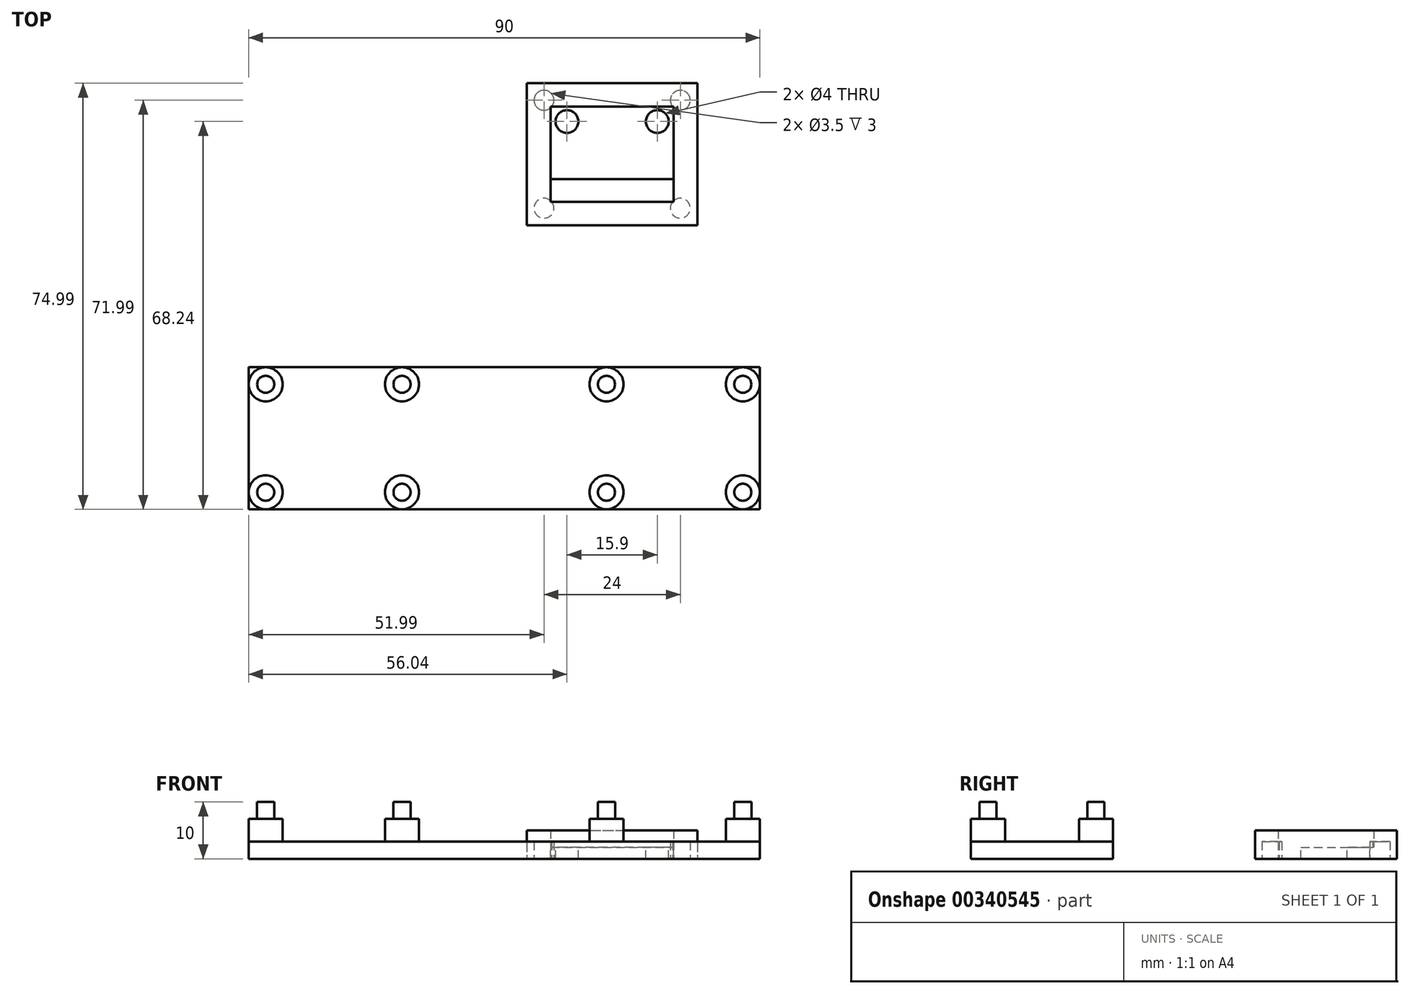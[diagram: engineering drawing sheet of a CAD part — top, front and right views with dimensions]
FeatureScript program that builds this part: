
annotation { "Feature Type Name" : "Feature", "Feature Type Description" : "" }
export const myFeature = defineFeature(function(context is Context, id is Id, definition is map)
    precondition{}
    {
        {
            var Q0;
            Q0=qCreatedBy(makeId("Top.planeOp"),FACE);
            var sketch = newSketch(context, id + "F0", { "sketchPlane" : qUnion([Q0])});
            skLineSegment(sketch, "E0.bottom", {"start": v(-15, 12.5) * mm, "end": v(15, 12.5) * mm});
            skLineSegment(sketch, "E0.top", {"start": v(-15, -12.5) * mm, "end": v(15, -12.5) * mm});
            skLineSegment(sketch, "E0.left", {"start": v(-15, 12.5) * mm, "end": v(-15, -12.5) * mm});
            skLineSegment(sketch, "E0.right", {"start": v(15, 12.5) * mm, "end": v(15, -12.5) * mm});
            skLineSegment(sketch, "E1.bottom", {"start": v(-10.8, 8.4) * mm, "end": v(10.8, 8.4) * mm});
            skLineSegment(sketch, "E1.top", {"start": v(-10.8, -8.4) * mm, "end": v(10.8, -8.4) * mm});
            skLineSegment(sketch, "E1.left", {"start": v(-10.8, 8.4) * mm, "end": v(-10.8, -8.4) * mm});
            skLineSegment(sketch, "E1.right", {"start": v(10.8, 8.4) * mm, "end": v(10.8, -8.4) * mm});
            skLineSegment(sketch, "E2", {"start": v(-15, 12.5) * mm, "end": v(15, -12.5) * mm, "construction": true});
            skLineSegment(sketch, "E3", {"start": v(-15, -12.5) * mm, "end": v(15, 12.5) * mm, "construction": true});
            skLineSegment(sketch, "E4", {"start": v(-10.8, 8.4) * mm, "end": v(10.8, -8.4) * mm, "construction": true});
            skLineSegment(sketch, "E5", {"start": v(-10.8, -8.4) * mm, "end": v(10.8, 8.4) * mm, "construction": true});
            skPoint(sketch, "E6", {"position": v(0, 0) * mm});
            skSolve(sketch);
        }
        {
            var Q0;
            Q0=qSketchRegion(id+"F0",true);
            extrude(context, id + "F1", {"entities" : qUnion([Q0]), "depth" : 5 * mm});
        }
        {
            var Q0;
            Q0=makeQuery(id+"F1.opExtrude","CAP_FACE",FACE,{"disambiguationData":[OSD([sQuery(id+"F0.wireOp",EDGE,"E0.bottom"),sQuery(id+"F0.wireOp",EDGE,"E0.top"),sQuery(id+"F0.wireOp",EDGE,"E0.left"),sQuery(id+"F0.wireOp",EDGE,"E0.right"),sQuery(id+"F0.wireOp",EDGE,"E1.bottom"),sQuery(id+"F0.wireOp",EDGE,"E1.top"),sQuery(id+"F0.wireOp",EDGE,"E1.left"),sQuery(id+"F0.wireOp",EDGE,"E1.right")])],"isStart":true});
            var sketch = newSketch(context, id + "F2", { "sketchPlane" : qUnion([Q0])});
            skLineSegment(sketch, "E7.0", {"start": v(-15, 12.5) * mm, "end": v(15, 12.5) * mm});
            skLineSegment(sketch, "E8.0", {"start": v(-15, -12.5) * mm, "end": v(-15, 12.5) * mm});
            skLineSegment(sketch, "E9.0", {"start": v(-15, -12.5) * mm, "end": v(15, -12.5) * mm});
            skLineSegment(sketch, "E10.0", {"start": v(15, -12.5) * mm, "end": v(15, 12.5) * mm});
            skSolve(sketch);
        }
        {
            var Q0;
            Q0=qSketchRegion(id+"F2",true);
            extrude(context, id + "F3", {"entities" : qUnion([Q0]), "operationType" : NewBodyOperationType.ADD, "oppositeDirection" : true, "depth" : 2 * mm});
        }
        {
            var Q0;
            Q0=makeQuery(id+"F3.opExtrude","CAP_FACE",FACE,{"disambiguationData":[OSD([sQuery(id+"F2.wireOp",EDGE,"E7.0"),sQuery(id+"F2.wireOp",EDGE,"E8.0"),sQuery(id+"F2.wireOp",EDGE,"E9.0"),sQuery(id+"F2.wireOp",EDGE,"E10.0")])],"isStart":false});
            var sketch = newSketch(context, id + "F4", { "sketchPlane" : qUnion([Q0])});
            skLineSegment(sketch, "E11.bottom", {"start": v(-10.8, -8.4) * mm, "end": v(10.8, -8.4) * mm});
            skLineSegment(sketch, "E11.top", {"start": v(-10.8, -4.4) * mm, "end": v(10.8, -4.4) * mm});
            skLineSegment(sketch, "E11.left", {"start": v(-10.8, -8.4) * mm, "end": v(-10.8, -4.4) * mm});
            skLineSegment(sketch, "E11.right", {"start": v(10.8, -8.4) * mm, "end": v(10.8, -4.4) * mm});
            skSolve(sketch);
        }
        {
            var Q0;
            Q0=qSketchRegion(id+"F4",true);
            extrude(context, id + "F5", {"entities" : qUnion([Q0]), "operationType" : NewBodyOperationType.REMOVE, "endBound" : BoundingType.UP_TO_NEXT, "oppositeDirection" : true, "depth" : 1.5 * mm});
        }
        {
            var Q0;
            Q0=makeQuery(id+"F3.opExtrude","CAP_FACE",FACE,{"disambiguationData":[OSD([sQuery(id+"F2.wireOp",EDGE,"E7.0"),sQuery(id+"F2.wireOp",EDGE,"E8.0"),sQuery(id+"F2.wireOp",EDGE,"E9.0"),sQuery(id+"F2.wireOp",EDGE,"E10.0")])],"isStart":false});
            var sketch = newSketch(context, id + "F6", { "sketchPlane" : qUnion([Q0])});
            skLineSegment(sketch, "E12", {"start": v(-7.95, 5.75) * mm, "end": v(7.95, 5.75) * mm, "construction": true});
            skCircle(sketch, "E13", {"center": v(-7.95, 5.75) * mm, "radius": 2 * mm});
            skCircle(sketch, "E14", {"center": v(7.95, 5.75) * mm, "radius": 2 * mm});
            skSolve(sketch);
        }
        {
            var Q0;
            Q0=qSketchRegion(id+"F6",true);
            extrude(context, id + "F7", {"entities" : qUnion([Q0]), "operationType" : NewBodyOperationType.REMOVE, "endBound" : BoundingType.UP_TO_NEXT, "oppositeDirection" : true, "depth" : 25 * mm});
        }
        {
            var Q0;
            Q0=qCreatedBy(makeId("Top.planeOp"),FACE);
            var sketch = newSketch(context, id + "F8", { "sketchPlane" : qUnion([Q0])});
            skLineSegment(sketch, "E15.bottom", {"start": v(-63.99, -37.5) * mm, "end": v(26.01, -37.5) * mm});
            skLineSegment(sketch, "E15.top", {"start": v(-63.99, -62.5) * mm, "end": v(26.01, -62.5) * mm});
            skLineSegment(sketch, "E15.left", {"start": v(-63.99, -37.5) * mm, "end": v(-63.99, -62.5) * mm});
            skLineSegment(sketch, "E15.right", {"start": v(26.01, -37.5) * mm, "end": v(26.01, -62.5) * mm});
            skSolve(sketch);
        }
        {
            var Q0;
            Q0=qSketchRegion(id+"F8",true);
            extrude(context, id + "F9", {"entities" : qUnion([Q0]), "depth" : 3 * mm});
        }
        {
            var Q0;
            Q0=makeQuery(id+"F9.opExtrude","CAP_FACE",FACE,{"disambiguationData":[OSD([sQuery(id+"F8.wireOp",EDGE,"E15.bottom"),sQuery(id+"F8.wireOp",EDGE,"E15.top"),sQuery(id+"F8.wireOp",EDGE,"E15.left"),sQuery(id+"F8.wireOp",EDGE,"E15.right")])],"isStart":false});
            var sketch = newSketch(context, id + "F10", { "sketchPlane" : qUnion([Q0])});
            skLineSegment(sketch, "E16.bottom", {"start": v(-60.99, -40.5) * mm, "end": v(-36.99, -40.5) * mm, "construction": true});
            skLineSegment(sketch, "E16.top", {"start": v(-60.99, -59.5) * mm, "end": v(-36.99, -59.5) * mm, "construction": true});
            skLineSegment(sketch, "E16.left", {"start": v(-60.99, -40.5) * mm, "end": v(-60.99, -59.5) * mm, "construction": true});
            skLineSegment(sketch, "E16.right", {"start": v(-36.99, -40.5) * mm, "end": v(-36.99, -59.5) * mm, "construction": true});
            skLineSegment(sketch, "E17.bottom", {"start": v(-0.99, -40.5) * mm, "end": v(23.01, -40.5) * mm, "construction": true});
            skLineSegment(sketch, "E17.top", {"start": v(-0.99, -59.5) * mm, "end": v(23.01, -59.5) * mm, "construction": true});
            skLineSegment(sketch, "E17.left", {"start": v(-0.99, -40.5) * mm, "end": v(-0.99, -59.5) * mm, "construction": true});
            skLineSegment(sketch, "E17.right", {"start": v(23.01, -40.5) * mm, "end": v(23.01, -59.5) * mm, "construction": true});
            skCircle(sketch, "E18", {"center": v(-60.99, -40.5) * mm, "radius": 3 * mm});
            skCircle(sketch, "E19", {"center": v(-36.99, -40.5) * mm, "radius": 3 * mm});
            skCircle(sketch, "E20", {"center": v(-36.99, -59.5) * mm, "radius": 3 * mm});
            skCircle(sketch, "E21", {"center": v(-60.99, -59.5) * mm, "radius": 3 * mm});
            skCircle(sketch, "E22", {"center": v(-0.99, -40.5) * mm, "radius": 3 * mm});
            skCircle(sketch, "E23", {"center": v(-0.99, -59.5) * mm, "radius": 3 * mm});
            skCircle(sketch, "E24", {"center": v(23.01, -40.5) * mm, "radius": 3 * mm});
            skCircle(sketch, "E25", {"center": v(23.01, -59.5) * mm, "radius": 3 * mm});
            skSolve(sketch);
        }
        {
            var Q0;
            Q0=qSketchRegion(id+"F10",true);
            extrude(context, id + "F11", {"entities" : qUnion([Q0]), "operationType" : NewBodyOperationType.ADD, "depth" : 4 * mm});
        }
        {
            var Q0;
            Q0=makeQuery(id+"F3.boolean.opBoolean","MERGE",FACE,{"derivedFrom":[makeQuery(id+"F1.opExtrude","CAP_FACE",FACE,{"disambiguationData":[OSD([sQuery(id+"F0.wireOp",EDGE,"E0.bottom"),sQuery(id+"F0.wireOp",EDGE,"E0.top"),sQuery(id+"F0.wireOp",EDGE,"E0.left"),sQuery(id+"F0.wireOp",EDGE,"E0.right"),sQuery(id+"F0.wireOp",EDGE,"E1.bottom"),sQuery(id+"F0.wireOp",EDGE,"E1.top"),sQuery(id+"F0.wireOp",EDGE,"E1.left"),sQuery(id+"F0.wireOp",EDGE,"E1.right")])],"isStart":true}),makeQuery(id+"F3.opExtrude","CAP_FACE",FACE,{"disambiguationData":[OSD([sQuery(id+"F2.wireOp",EDGE,"E7.0"),sQuery(id+"F2.wireOp",EDGE,"E8.0"),sQuery(id+"F2.wireOp",EDGE,"E9.0"),sQuery(id+"F2.wireOp",EDGE,"E10.0")])],"isStart":true})]});
            var sketch = newSketch(context, id + "F12", { "sketchPlane" : qUnion([Q0])});
            skLineSegment(sketch, "E26.bottom", {"start": v(-12, 9.5) * mm, "end": v(12, 9.5) * mm, "construction": true});
            skLineSegment(sketch, "E26.top", {"start": v(-12, -9.5) * mm, "end": v(12, -9.5) * mm, "construction": true});
            skLineSegment(sketch, "E26.left", {"start": v(-12, 9.5) * mm, "end": v(-12, -9.5) * mm, "construction": true});
            skLineSegment(sketch, "E26.right", {"start": v(12, 9.5) * mm, "end": v(12, -9.5) * mm, "construction": true});
            skCircle(sketch, "E27", {"center": v(-12, 9.5) * mm, "radius": 1.75 * mm});
            skCircle(sketch, "E28", {"center": v(12, 9.5) * mm, "radius": 1.75 * mm});
            skCircle(sketch, "E29", {"center": v(12, -9.5) * mm, "radius": 1.75 * mm});
            skCircle(sketch, "E30", {"center": v(-12, -9.5) * mm, "radius": 1.75 * mm});
            skSolve(sketch);
        }
        {
            var Q0;
            Q0 = qSketchRegion(id + "F12", true);
            extrude(context, id + "F13", {"entities" : qUnion([Q0]), "operationType" : NewBodyOperationType.REMOVE, "oppositeDirection" : true, "depth" : 3 * mm});
        }
        {
            var Q0;
            Q0=makeQuery(id+"F11.opExtrude","CAP_FACE",FACE,{"disambiguationData":[OSD([sQuery(id+"F10.wireOp",EDGE,"E18")])],"isStart":false});
            var sketch = newSketch(context, id + "F14", { "sketchPlane" : qUnion([Q0])});
            skCircle(sketch, "E31", {"center": v(-60.99, -40.5) * mm, "radius": 1.5 * mm});
            skCircle(sketch, "E32.0.0", {"center": v(-36.99, -40.5) * mm, "radius": 3 * mm, "construction": true});
            skCircle(sketch, "E33.0.0", {"center": v(-36.99, -59.5) * mm, "radius": 3 * mm, "construction": true});
            skCircle(sketch, "E34.0.0", {"center": v(-60.99, -59.5) * mm, "radius": 3 * mm, "construction": true});
            skCircle(sketch, "E35.0.0", {"center": v(-0.99, -40.5) * mm, "radius": 3 * mm, "construction": true});
            skCircle(sketch, "E36.0.0", {"center": v(23.01, -40.5) * mm, "radius": 3 * mm, "construction": true});
            skCircle(sketch, "E37.0.0", {"center": v(23.01, -59.5) * mm, "radius": 3 * mm, "construction": true});
            skCircle(sketch, "E38.0.0", {"center": v(-0.99, -59.5) * mm, "radius": 3 * mm, "construction": true});
            skCircle(sketch, "E39", {"center": v(-60.99, -59.5) * mm, "radius": 1.5 * mm});
            skCircle(sketch, "E40", {"center": v(-36.99, -40.5) * mm, "radius": 1.5 * mm});
            skCircle(sketch, "E41", {"center": v(-36.99, -59.5) * mm, "radius": 1.5 * mm});
            skCircle(sketch, "E42", {"center": v(-0.99, -40.5) * mm, "radius": 1.5 * mm});
            skCircle(sketch, "E43", {"center": v(-0.99, -59.5) * mm, "radius": 1.5 * mm});
            skCircle(sketch, "E44", {"center": v(23.01, -40.5) * mm, "radius": 1.5 * mm});
            skCircle(sketch, "E45", {"center": v(23.01, -59.5) * mm, "radius": 1.5 * mm});
            skSolve(sketch);
        }
        {
            var Q0;
            Q0 = qSketchRegion(id + "F14", true);
            extrude(context, id + "F15", {"entities" : qUnion([Q0]), "operationType" : NewBodyOperationType.ADD, "depth" : 3 * mm});
        }
    });
